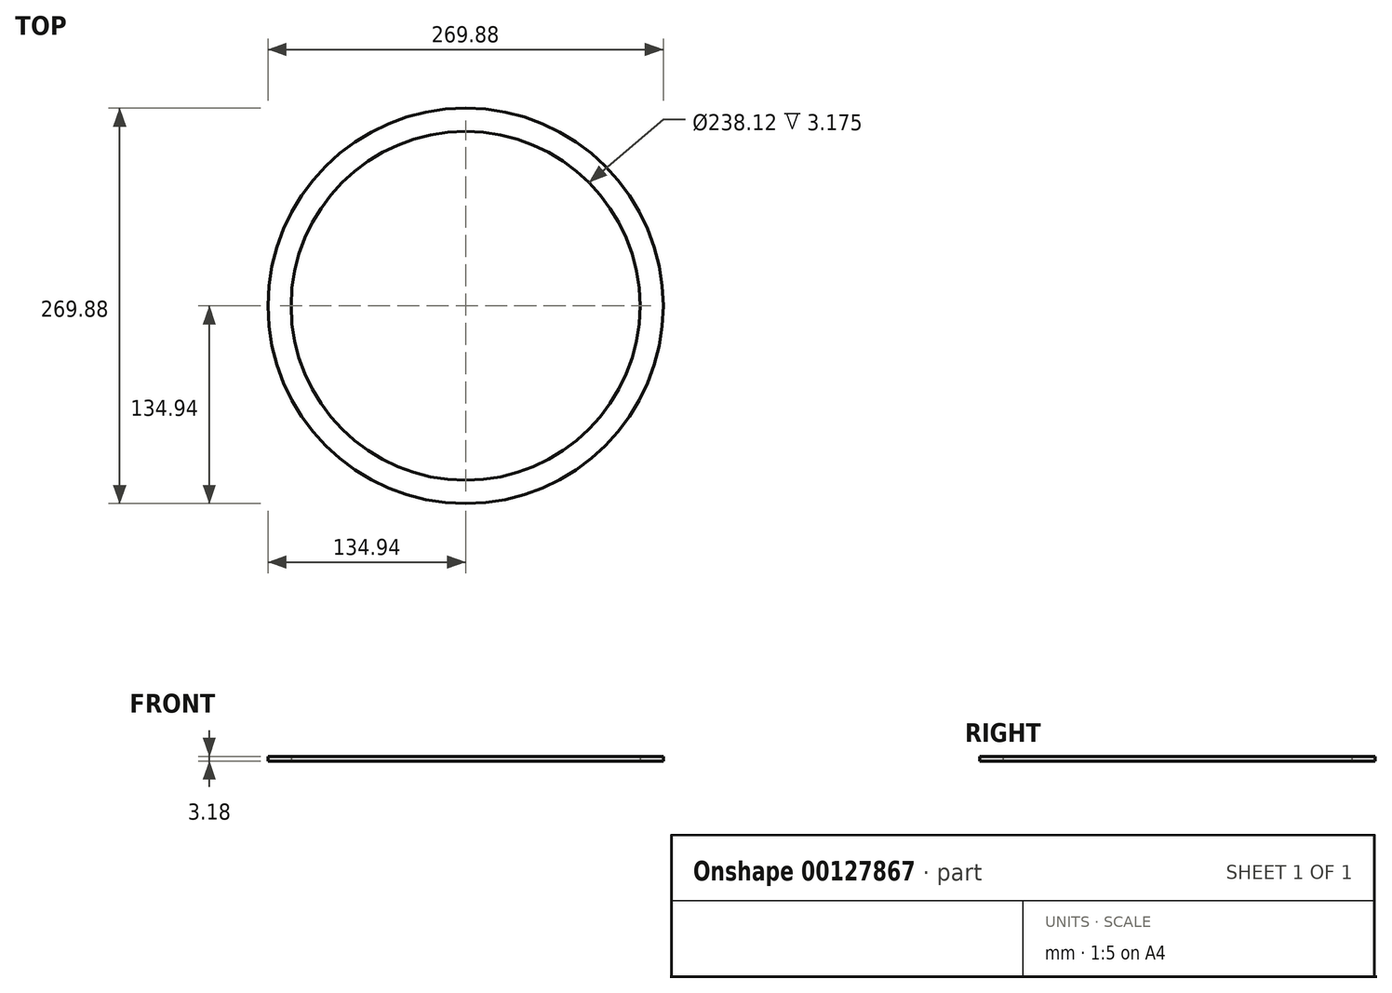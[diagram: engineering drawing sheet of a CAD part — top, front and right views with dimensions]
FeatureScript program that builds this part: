
annotation { "Feature Type Name" : "Feature", "Feature Type Description" : "" }
export const myFeature = defineFeature(function(context is Context, id is Id, definition is map)
    precondition{}
    {
        {
            var Q0;
            Q0=qCreatedBy(makeId("Top.planeOp"),FACE);
            var sketch = newSketch(context, id + "F0", { "sketchPlane" : qUnion([Q0])});
            skCircle(sketch, "E0", {"center": v(0, 0) * mm, "radius": 119.06 * mm});
            skCircle(sketch, "E1", {"center": v(0, 0) * mm, "radius": 134.94 * mm});
            skSolve(sketch);
        }
        {
            var Q0;
            Q0=makeQuery(id+"F0.imprint","IMPRINT",FACE,{"disambiguationData":[TD([[makeQuery(id+"F0.imprint","IMPRINT",EDGE,{"derivedFrom":sQuery(id+"F0.wireOp",EDGE,"E0")}),-1.0]])]});
            extrude(context, id + "F1", {"entities" : qUnion([Q0]), "depth" : 3.17 * mm});
        }
    });
